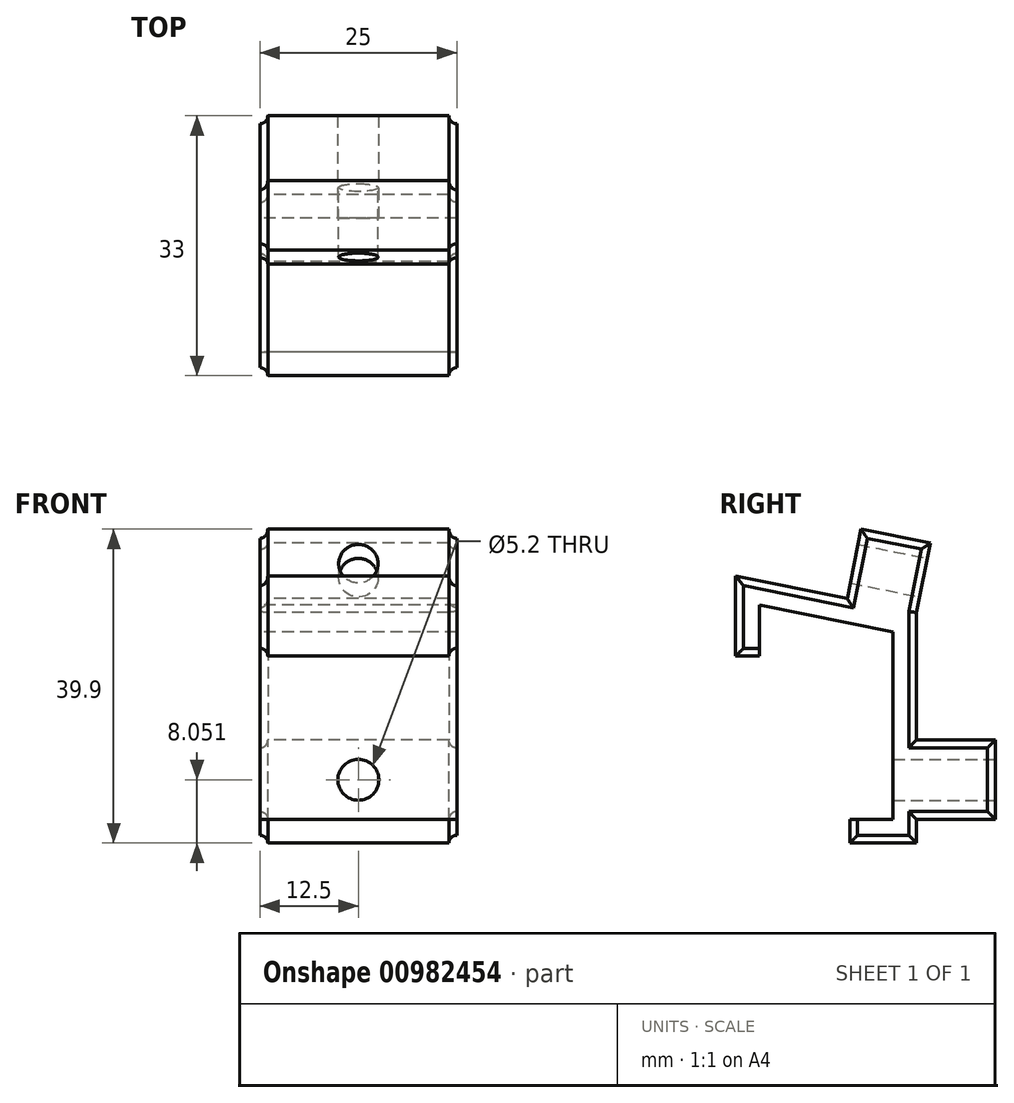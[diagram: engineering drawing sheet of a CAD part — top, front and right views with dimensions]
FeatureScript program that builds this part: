
annotation { "Feature Type Name" : "Feature", "Feature Type Description" : "" }
export const myFeature = defineFeature(function(context is Context, id is Id, definition is map)
    precondition{}
    {
        {
            var Q0;
            Q0=qCreatedBy(makeId("Right.planeOp"),FACE);
            var sketch = newSketch(context, id + "F0", { "sketchPlane" : qUnion([Q0])});
            skLineSegment(sketch, "E0.top", {"start": v(3.24, -5.36) * mm, "end": v(8.74, -5.36) * mm});
            skLineSegment(sketch, "E0.right", {"start": v(8.74, 18.5) * mm, "end": v(8.74, -5.36) * mm});
            skLineSegment(sketch, "E1", {"start": v(-5.7, 21.4) * mm, "end": v(8.74, 18.5) * mm});
            skLineSegment(sketch, "E2", {"start": v(8.74, -5.36) * mm, "end": v(3.24, -5.36) * mm});
            skLineSegment(sketch, "E3.0", {"start": v(11.74, -8.36) * mm, "end": v(3.24, -8.36) * mm});
            skLineSegment(sketch, "E3.1", {"start": v(11.74, 20.95) * mm, "end": v(11.74, -8.36) * mm});
            skLineSegment(sketch, "E3.2", {"start": v(-8.7, 25.05) * mm, "end": v(11.74, 20.95) * mm});
            skLineSegment(sketch, "E4", {"start": v(-8.7, 15.4) * mm, "end": v(-8.26, 15.4) * mm});
            skLineSegment(sketch, "E5", {"start": v(11.74, 20.95) * mm, "end": v(13.51, 29.77) * mm});
            skLineSegment(sketch, "E6", {"start": v(13.51, 29.77) * mm, "end": v(4.69, 31.54) * mm});
            skLineSegment(sketch, "E7", {"start": v(4.69, 31.54) * mm, "end": v(2.91, 22.72) * mm});
            skLineSegment(sketch, "E8", {"start": v(11.74, -5.36) * mm, "end": v(21.74, -5.36) * mm});
            skLineSegment(sketch, "E9", {"start": v(21.74, -5.36) * mm, "end": v(21.74, 4.74) * mm});
            skLineSegment(sketch, "E10", {"start": v(21.74, 4.74) * mm, "end": v(11.74, 4.74) * mm});
            skLineSegment(sketch, "E11", {"start": v(11.74, 4.74) * mm, "end": v(11.74, -5.36) * mm});
            skLineSegment(sketch, "E12", {"start": v(3.24, -5.36) * mm, "end": v(3.24, -8.36) * mm});
            skLineSegment(sketch, "E13", {"start": v(3.24, -8.36) * mm, "end": v(8.74, -8.36) * mm});
            skPoint(sketch, "E14.orphan", {"position": v(-7.76, -5.36) * mm});
            skLineSegment(sketch, "E15", {"start": v(-5.7, 21.4) * mm, "end": v(-8.26, 21.9) * mm});
            skLineSegment(sketch, "E16", {"start": v(-8.7, 25.05) * mm, "end": v(-11.26, 25.57) * mm});
            skLineSegment(sketch, "E17", {"start": v(-8.7, 15.4) * mm, "end": v(-11.26, 15.4) * mm});
            skLineSegment(sketch, "E18", {"start": v(-8.26, 21.9) * mm, "end": v(-8.26, 15.4) * mm});
            skLineSegment(sketch, "E19", {"start": v(-11.26, 25.57) * mm, "end": v(-11.26, 15.4) * mm});
            skLineSegment(sketch, "E20", {"start": v(-8.26, 21.9) * mm, "end": v(-8.26, 24.97) * mm});
            skSolve(sketch);
        }
        {
            var Q0;
            Q0 = qSketchRegion(id + "F0", true);
            extrude(context, id + "F1", {"entities" : qUnion([Q0]), "depth" : 25 * mm, "offsetDistance" : 25 * mm});
        }
        {
            var Q0;
            Q0=makeQuery(id+"F1.opExtrude","SWEPT_FACE",FACE,{"disambiguationData":[OSD([sQuery(id+"F0.wireOp",EDGE,"E5")])]});
            var sketch = newSketch(context, id + "F2", { "sketchPlane" : qUnion([Q0])});
            skLineSegment(sketch, "E21", {"start": v(-12.5, 23.66) * mm, "end": v(-12.5, 38.4) * mm, "construction": true});
            skPoint(sketch, "E21.startSnap0", {"position": v(-12.5, 22.85) * mm});
            skLineSegment(sketch, "E22", {"start": v(-25, 27.35) * mm, "end": v(3.97, 27.35) * mm, "construction": true});
            skCircle(sketch, "E23", {"center": v(-12.5, 27.35) * mm, "radius": 2.5 * mm});
            skLineSegment(sketch, "E24.bottom", {"start": v(-12.5, 31.85) * mm, "end": v(-10.5, 31.85) * mm});
            skLineSegment(sketch, "E24.top", {"start": v(-12.5, 31.85) * mm, "end": v(-10.5, 31.85) * mm});
            skLineSegment(sketch, "E24.left", {"start": v(-12.5, 31.85) * mm, "end": v(-12.5, 31.85) * mm});
            skLineSegment(sketch, "E24.right", {"start": v(-10.5, 31.85) * mm, "end": v(-10.5, 31.85) * mm});
            skLineSegment(sketch, "E25.top", {"start": v(-10.5, 28.85) * mm, "end": v(-10.5, 28.85) * mm});
            skLineSegment(sketch, "E25.left", {"start": v(-10.5, 31.85) * mm, "end": v(-10.5, 28.85) * mm});
            skLineSegment(sketch, "E25.right", {"start": v(-10.5, 31.85) * mm, "end": v(-10.5, 28.85) * mm});
            skLineSegment(sketch, "E26", {"start": v(-12.5, 31.85) * mm, "end": v(-14.5, 31.85) * mm});
            skLineSegment(sketch, "E27", {"start": v(-14.5, 31.85) * mm, "end": v(-14.5, 28.85) * mm});
            skSolve(sketch);
        }
        {
            var Q0;
            {var subQ0=sQuery(id+"F2.wireOp",EDGE,"E23");var subQ1=makeQuery(id+"F2.imprint","INTERSECT",VERTEX,{"derivedFrom":[subQ0,sQuery(id+"F2.wireOp",EDGE,"E25.right")]});Q0=makeQuery(id+"F2.imprint","IMPRINT",FACE,{"disambiguationData":[TD([[makeQuery(id+"F2.imprint","IMPRINT",EDGE,{"disambiguationData":[TD([[subQ1,-1.0]])],"derivedFrom":subQ0}),1.0]])]});}
            var Q1;
            Q1=makeQuery(id+"F2.imprint","IMPRINT",FACE,{"disambiguationData":[TD([[makeQuery(id+"F2.imprint","IMPRINT",EDGE,{"derivedFrom":sQuery(id+"F2.wireOp",EDGE,"E24.top")}),-1.0]])]});
            extrude(context, id + "F3", {"entities" : qUnion([Q0, Q1]), "operationType" : NewBodyOperationType.REMOVE, "endBound" : BoundingType.THROUGH_ALL, "oppositeDirection" : true, "depth" : 25 * mm, "offsetDistance" : 25 * mm});
        }
        {
            var Q0;
            Q0=makeQuery(id+"F1.opExtrude","SWEPT_FACE",FACE,{"disambiguationData":[OSD([sQuery(id+"F0.wireOp",EDGE,"E9")])]});
            var sketch = newSketch(context, id + "F4", { "sketchPlane" : qUnion([Q0])});
            skLineSegment(sketch, "E28", {"start": v(-12.5, 4.74) * mm, "end": v(-12.5, -5.36) * mm, "construction": true});
            skLineSegment(sketch, "E29", {"start": v(-25, -0.3) * mm, "end": v(0, -0.3) * mm, "construction": true});
            skCircle(sketch, "E30", {"center": v(-12.5, -0.3) * mm, "radius": 2.6 * mm});
            skSolve(sketch);
        }
        {
            var Q0;
            Q0=makeQuery(id+"F4.imprint","IMPRINT",FACE,{"disambiguationData":[TD([[makeQuery(id+"F4.imprint","IMPRINT",EDGE,{"derivedFrom":sQuery(id+"F4.wireOp",EDGE,"E30")}),1.0]])]});
            extrude(context, id + "F5", {"entities" : qUnion([Q0]), "operationType" : NewBodyOperationType.REMOVE, "endBound" : BoundingType.THROUGH_ALL, "oppositeDirection" : true, "depth" : 25 * mm, "offsetDistance" : 25 * mm});
        }
        {
            var Q0;
            Q0=makeQuery(id+"F1.opExtrude","CAP_FACE",FACE,{"disambiguationData":[OSD([sQuery(id+"F0.wireOp",EDGE,"E0.right"),sQuery(id+"F0.wireOp",EDGE,"E1"),sQuery(id+"F0.wireOp",EDGE,"n86n0oZb-3QEX-ZodZ-O8e6-zm0sU3kRzoy1"),sQuery(id+"F0.wireOp",EDGE,"E3.0"),sQuery(id+"F0.wireOp",EDGE,"E3.1"),sQuery(id+"F0.wireOp",EDGE,"E3.2"),sQuery(id+"F0.wireOp",EDGE,"E3.3"),sQuery(id+"F0.wireOp",EDGE,"E4"),sQuery(id+"F0.wireOp",EDGE,"E5"),sQuery(id+"F0.wireOp",EDGE,"E6"),sQuery(id+"F0.wireOp",EDGE,"E7"),sQuery(id+"F0.wireOp",EDGE,"E8"),sQuery(id+"F0.wireOp",EDGE,"E9"),sQuery(id+"F0.wireOp",EDGE,"E10"),sQuery(id+"F0.wireOp",EDGE,"E2"),sQuery(id+"F0.wireOp",EDGE,"E12"),sQuery(id+"F0.wireOp",EDGE,"E13")])],"isStart":true});
            var sketch = newSketch(context, id + "F6", { "sketchPlane" : qUnion([Q0])});
            skLineSegment(sketch, "E31", {"start": v(8.26, 15.4) * mm, "end": v(-2.91, 22.72) * mm});
            skLineSegment(sketch, "E32", {"start": v(-2.91, 22.72) * mm, "end": v(-2.91, 22.72) * mm});
            skLineSegment(sketch, "E33", {"start": v(-2.91, 22.72) * mm, "end": v(-4.69, 31.54) * mm});
            skLineSegment(sketch, "E34", {"start": v(-4.69, 31.54) * mm, "end": v(-13.51, 29.77) * mm});
            skLineSegment(sketch, "E35", {"start": v(-13.51, 29.77) * mm, "end": v(-11.74, 20.95) * mm});
            skLineSegment(sketch, "E36", {"start": v(-11.74, 20.95) * mm, "end": v(-11.74, 4.74) * mm});
            skLineSegment(sketch, "E37", {"start": v(-11.74, 4.74) * mm, "end": v(-21.74, 4.74) * mm});
            skLineSegment(sketch, "E38", {"start": v(-21.74, 4.74) * mm, "end": v(-21.74, -5.36) * mm});
            skLineSegment(sketch, "E39", {"start": v(-21.74, -5.36) * mm, "end": v(-11.74, -5.36) * mm});
            skLineSegment(sketch, "E40", {"start": v(-11.74, -5.36) * mm, "end": v(-11.74, -8.36) * mm});
            skLineSegment(sketch, "E41", {"start": v(-11.74, -8.36) * mm, "end": v(-3.24, -8.36) * mm});
            skLineSegment(sketch, "E42.0", {"start": v(-10.74, -7.36) * mm, "end": v(-3.24, -7.36) * mm});
            skLineSegment(sketch, "E42.1", {"start": v(-5.47, 30.37) * mm, "end": v(-12.33, 28.99) * mm});
            skLineSegment(sketch, "E42.2", {"start": v(-3.81, 22.11) * mm, "end": v(-5.47, 30.37) * mm});
            skLineSegment(sketch, "E42.3", {"start": v(-0.9, 20.2) * mm, "end": v(-3.81, 22.11) * mm});
            skLineSegment(sketch, "E42.4", {"start": v(6.44, 15.4) * mm, "end": v(-0.9, 20.2) * mm});
            skLineSegment(sketch, "E42.5", {"start": v(-12.33, 28.99) * mm, "end": v(-10.74, 21.05) * mm});
            skLineSegment(sketch, "E42.6", {"start": v(-10.74, 21.05) * mm, "end": v(-10.74, 3.74) * mm});
            skLineSegment(sketch, "E42.7", {"start": v(-10.74, 3.74) * mm, "end": v(-20.74, 3.74) * mm});
            skLineSegment(sketch, "E42.8", {"start": v(-20.74, 3.74) * mm, "end": v(-20.74, -4.36) * mm});
            skLineSegment(sketch, "E42.9", {"start": v(-20.74, -4.36) * mm, "end": v(-10.74, -4.36) * mm});
            skLineSegment(sketch, "E42.10", {"start": v(-10.74, -4.36) * mm, "end": v(-10.74, -7.36) * mm});
            skLineSegment(sketch, "E43", {"start": v(-3.24, -7.36) * mm, "end": v(-3.24, -8.36) * mm});
            skLineSegment(sketch, "E44", {"start": v(8.26, 15.4) * mm, "end": v(6.44, 15.4) * mm});
            skSolve(sketch);
        }
        {
            var Q0;
            Q0=makeQuery(id+"F6.imprint","IMPRINT",FACE,{"disambiguationData":[TD([[makeQuery(id+"F6.imprint","IMPRINT",EDGE,{"derivedFrom":sQuery(id+"F6.wireOp",EDGE,"E31")}),-1.0]])]});
            extrude(context, id + "F7", {"entities" : qUnion([Q0]), "operationType" : NewBodyOperationType.REMOVE, "oppositeDirection" : true, "depth" : 1 * mm, "offsetDistance" : 25 * mm});
        }
        {
            var Q0;
            Q0=makeQuery(id+"F1.opExtrude","CAP_FACE",FACE,{"disambiguationData":[OSD([sQuery(id+"F0.wireOp",EDGE,"E0.right"),sQuery(id+"F0.wireOp",EDGE,"E1"),sQuery(id+"F0.wireOp",EDGE,"E3.0"),sQuery(id+"F0.wireOp",EDGE,"E3.1"),sQuery(id+"F0.wireOp",EDGE,"E3.2"),sQuery(id+"F0.wireOp",EDGE,"E4"),sQuery(id+"F0.wireOp",EDGE,"E5"),sQuery(id+"F0.wireOp",EDGE,"E6"),sQuery(id+"F0.wireOp",EDGE,"E7"),sQuery(id+"F0.wireOp",EDGE,"E8"),sQuery(id+"F0.wireOp",EDGE,"E9"),sQuery(id+"F0.wireOp",EDGE,"E10"),sQuery(id+"F0.wireOp",EDGE,"E2"),sQuery(id+"F0.wireOp",EDGE,"E12"),sQuery(id+"F0.wireOp",EDGE,"E13"),sQuery(id+"F0.wireOp",EDGE,"E15"),sQuery(id+"F0.wireOp",EDGE,"E16"),sQuery(id+"F0.wireOp",EDGE,"E17"),sQuery(id+"F0.wireOp",EDGE,"E18"),sQuery(id+"F0.wireOp",EDGE,"E19")])],"isStart":false});
            var sketch = newSketch(context, id + "F8", { "sketchPlane" : qUnion([Q0])});
            skLineSegment(sketch, "E45", {"start": v(-8.26, 15.4) * mm, "end": v(-11.26, 15.4) * mm});
            skLineSegment(sketch, "E46", {"start": v(-11.26, 15.4) * mm, "end": v(-11.26, 25.57) * mm});
            skLineSegment(sketch, "E47", {"start": v(-11.26, 25.57) * mm, "end": v(2.91, 22.72) * mm});
            skLineSegment(sketch, "E48", {"start": v(2.91, 22.72) * mm, "end": v(4.69, 31.54) * mm});
            skLineSegment(sketch, "E49", {"start": v(4.69, 31.54) * mm, "end": v(13.51, 29.77) * mm});
            skLineSegment(sketch, "E50", {"start": v(13.51, 29.77) * mm, "end": v(11.74, 20.95) * mm});
            skLineSegment(sketch, "E51", {"start": v(11.74, 20.95) * mm, "end": v(11.74, 4.74) * mm});
            skLineSegment(sketch, "E52", {"start": v(11.74, 4.74) * mm, "end": v(21.74, 4.74) * mm});
            skLineSegment(sketch, "E53", {"start": v(21.74, 4.74) * mm, "end": v(21.74, -5.36) * mm});
            skLineSegment(sketch, "E54", {"start": v(21.74, -5.36) * mm, "end": v(11.74, -5.36) * mm});
            skLineSegment(sketch, "E55", {"start": v(11.74, -5.36) * mm, "end": v(11.74, -8.36) * mm});
            skLineSegment(sketch, "E56", {"start": v(11.74, -8.36) * mm, "end": v(3.24, -8.36) * mm});
            skLineSegment(sketch, "E57", {"start": v(3.24, -8.36) * mm, "end": v(3.24, -5.36) * mm});
            skLineSegment(sketch, "E58.0", {"start": v(4.24, -7.36) * mm, "end": v(4.24, -5.36) * mm});
            skLineSegment(sketch, "E58.1", {"start": v(10.74, -7.36) * mm, "end": v(4.24, -7.36) * mm});
            skLineSegment(sketch, "E58.2", {"start": v(10.74, -4.36) * mm, "end": v(10.74, -7.36) * mm});
            skLineSegment(sketch, "E58.3", {"start": v(3.7, 21.54) * mm, "end": v(5.47, 30.37) * mm});
            skLineSegment(sketch, "E58.4", {"start": v(-10.26, 24.35) * mm, "end": v(3.7, 21.54) * mm});
            skLineSegment(sketch, "E58.5", {"start": v(-10.26, 16.4) * mm, "end": v(-10.26, 24.35) * mm});
            skLineSegment(sketch, "E58.6", {"start": v(-8.26, 16.4) * mm, "end": v(-10.26, 16.4) * mm});
            skLineSegment(sketch, "E58.7", {"start": v(5.47, 30.37) * mm, "end": v(12.33, 28.99) * mm});
            skLineSegment(sketch, "E58.8", {"start": v(12.33, 28.99) * mm, "end": v(10.74, 21.05) * mm});
            skLineSegment(sketch, "E58.9", {"start": v(10.74, 21.05) * mm, "end": v(10.74, 3.74) * mm});
            skLineSegment(sketch, "E58.10", {"start": v(10.74, 3.74) * mm, "end": v(20.74, 3.74) * mm});
            skLineSegment(sketch, "E58.11", {"start": v(20.74, 3.74) * mm, "end": v(20.74, -4.36) * mm});
            skLineSegment(sketch, "E58.12", {"start": v(20.74, -4.36) * mm, "end": v(10.74, -4.36) * mm});
            skLineSegment(sketch, "E59", {"start": v(-8.26, 16.4) * mm, "end": v(-8.26, 15.4) * mm});
            skLineSegment(sketch, "E60", {"start": v(3.24, -5.36) * mm, "end": v(4.24, -5.36) * mm});
            skSolve(sketch);
        }
        {
            var Q0;
            Q0=makeQuery(id+"F8.imprint","IMPRINT",FACE,{"disambiguationData":[TD([[makeQuery(id+"F8.imprint","IMPRINT",EDGE,{"derivedFrom":sQuery(id+"F8.wireOp",EDGE,"E45")}),-1.0]])]});
            extrude(context, id + "F9", {"entities" : qUnion([Q0]), "operationType" : NewBodyOperationType.REMOVE, "oppositeDirection" : true, "depth" : 1 * mm, "offsetDistance" : 25 * mm});
        }
        {
            var Q0;
            Q0=makeQuery(id+"F1.opExtrude","CAP_FACE",FACE,{"disambiguationData":[OSD([sQuery(id+"F0.wireOp",EDGE,"E0.right"),sQuery(id+"F0.wireOp",EDGE,"E1"),sQuery(id+"F0.wireOp",EDGE,"E3.0"),sQuery(id+"F0.wireOp",EDGE,"E3.1"),sQuery(id+"F0.wireOp",EDGE,"E3.2"),sQuery(id+"F0.wireOp",EDGE,"E4"),sQuery(id+"F0.wireOp",EDGE,"E5"),sQuery(id+"F0.wireOp",EDGE,"E6"),sQuery(id+"F0.wireOp",EDGE,"E7"),sQuery(id+"F0.wireOp",EDGE,"E8"),sQuery(id+"F0.wireOp",EDGE,"E9"),sQuery(id+"F0.wireOp",EDGE,"E10"),sQuery(id+"F0.wireOp",EDGE,"E2"),sQuery(id+"F0.wireOp",EDGE,"E12"),sQuery(id+"F0.wireOp",EDGE,"E13"),sQuery(id+"F0.wireOp",EDGE,"E15"),sQuery(id+"F0.wireOp",EDGE,"E16"),sQuery(id+"F0.wireOp",EDGE,"E17"),sQuery(id+"F0.wireOp",EDGE,"E18"),sQuery(id+"F0.wireOp",EDGE,"E19")])],"isStart":true});
            var sketch = newSketch(context, id + "F10", { "sketchPlane" : qUnion([Q0])});
            skLineSegment(sketch, "E61", {"start": v(8.26, 15.4) * mm, "end": v(11.26, 15.4) * mm});
            skLineSegment(sketch, "E62", {"start": v(11.26, 15.4) * mm, "end": v(11.26, 25.57) * mm});
            skLineSegment(sketch, "E63", {"start": v(11.26, 25.57) * mm, "end": v(-2.91, 22.72) * mm});
            skLineSegment(sketch, "E64", {"start": v(-2.91, 22.72) * mm, "end": v(-4.69, 31.54) * mm});
            skLineSegment(sketch, "E65", {"start": v(-4.69, 31.54) * mm, "end": v(-13.51, 29.77) * mm});
            skLineSegment(sketch, "E66", {"start": v(-13.51, 29.77) * mm, "end": v(-11.74, 20.95) * mm});
            skLineSegment(sketch, "E67", {"start": v(-11.74, 20.95) * mm, "end": v(-11.74, 4.74) * mm});
            skLineSegment(sketch, "E68", {"start": v(-11.74, 4.74) * mm, "end": v(-21.74, 4.74) * mm});
            skLineSegment(sketch, "E69", {"start": v(-21.74, 4.74) * mm, "end": v(-21.74, -5.36) * mm});
            skLineSegment(sketch, "E70", {"start": v(-21.74, -5.36) * mm, "end": v(-11.74, -5.36) * mm});
            skLineSegment(sketch, "E71", {"start": v(-11.74, -5.36) * mm, "end": v(-11.74, -8.36) * mm});
            skLineSegment(sketch, "E72", {"start": v(-11.74, -8.36) * mm, "end": v(-3.24, -8.36) * mm});
            skLineSegment(sketch, "E73", {"start": v(-3.24, -8.36) * mm, "end": v(-3.24, -5.36) * mm});
            skLineSegment(sketch, "E74.0", {"start": v(-4.24, -7.36) * mm, "end": v(-4.24, -5.36) * mm});
            skLineSegment(sketch, "E74.1", {"start": v(-10.74, -7.36) * mm, "end": v(-4.24, -7.36) * mm});
            skLineSegment(sketch, "E74.2", {"start": v(-10.74, -4.36) * mm, "end": v(-10.74, -7.36) * mm});
            skLineSegment(sketch, "E74.3", {"start": v(-3.7, 21.54) * mm, "end": v(-5.47, 30.37) * mm});
            skLineSegment(sketch, "E74.4", {"start": v(10.26, 24.35) * mm, "end": v(-3.7, 21.54) * mm});
            skLineSegment(sketch, "E74.5", {"start": v(10.26, 16.4) * mm, "end": v(10.26, 24.35) * mm});
            skLineSegment(sketch, "E74.6", {"start": v(8.26, 16.4) * mm, "end": v(10.26, 16.4) * mm});
            skLineSegment(sketch, "E74.7", {"start": v(-5.47, 30.37) * mm, "end": v(-12.33, 28.99) * mm});
            skLineSegment(sketch, "E74.8", {"start": v(-12.33, 28.99) * mm, "end": v(-10.74, 21.05) * mm});
            skLineSegment(sketch, "E74.9", {"start": v(-10.74, 21.05) * mm, "end": v(-10.74, 3.74) * mm});
            skLineSegment(sketch, "E74.10", {"start": v(-10.74, 3.74) * mm, "end": v(-20.74, 3.74) * mm});
            skLineSegment(sketch, "E74.11", {"start": v(-20.74, 3.74) * mm, "end": v(-20.74, -4.36) * mm});
            skLineSegment(sketch, "E74.12", {"start": v(-20.74, -4.36) * mm, "end": v(-10.74, -4.36) * mm});
            skLineSegment(sketch, "E75.0", {"start": v(-3.74, 14.4) * mm, "end": v(3.26, 15.8) * mm});
            skLineSegment(sketch, "E75.1", {"start": v(-3.74, -0.36) * mm, "end": v(-3.74, 14.4) * mm});
            skLineSegment(sketch, "E75.2", {"start": v(1.76, -0.36) * mm, "end": v(-3.74, -0.36) * mm});
            skLineSegment(sketch, "E75.3", {"start": v(1.76, -13.36) * mm, "end": v(1.76, -0.36) * mm});
            skLineSegment(sketch, "E75.4", {"start": v(-16.74, -13.36) * mm, "end": v(1.76, -13.36) * mm});
            skLineSegment(sketch, "E75.5", {"start": v(3.26, 15.8) * mm, "end": v(3.26, 10.4) * mm});
            skLineSegment(sketch, "E75.6", {"start": v(-16.74, -10.36) * mm, "end": v(-16.74, -13.36) * mm});
            skLineSegment(sketch, "E75.7", {"start": v(1, 28.6) * mm, "end": v(-0.77, 37.43) * mm});
            skLineSegment(sketch, "E75.8", {"start": v(16.26, 31.67) * mm, "end": v(1, 28.6) * mm});
            skLineSegment(sketch, "E75.9", {"start": v(16.26, 10.4) * mm, "end": v(16.26, 31.67) * mm});
            skLineSegment(sketch, "E75.10", {"start": v(3.26, 10.4) * mm, "end": v(16.26, 10.4) * mm});
            skLineSegment(sketch, "E75.11", {"start": v(-0.77, 37.43) * mm, "end": v(-19.4, 33.69) * mm});
            skLineSegment(sketch, "E75.12", {"start": v(-19.4, 33.69) * mm, "end": v(-16.74, 20.45) * mm});
            skLineSegment(sketch, "E75.13", {"start": v(-16.74, 20.45) * mm, "end": v(-16.74, 9.74) * mm});
            skLineSegment(sketch, "E75.14", {"start": v(-16.74, 9.74) * mm, "end": v(-26.74, 9.74) * mm});
            skLineSegment(sketch, "E75.15", {"start": v(-26.74, 9.74) * mm, "end": v(-26.74, -10.36) * mm});
            skLineSegment(sketch, "E75.16", {"start": v(-26.74, -10.36) * mm, "end": v(-16.74, -10.36) * mm});
            skLineSegment(sketch, "E76", {"start": v(8.26, 16.4) * mm, "end": v(8.26, 15.4) * mm});
            skLineSegment(sketch, "E77", {"start": v(-4.24, -5.36) * mm, "end": v(-3.24, -5.36) * mm});
            skSolve(sketch);
        }
        {
            var Q0;
            Q0=makeQuery(id+"F10.imprint","IMPRINT",FACE,{"disambiguationData":[TD([[makeQuery(id+"F10.imprint","IMPRINT",EDGE,{"derivedFrom":sQuery(id+"F10.wireOp",EDGE,"E61")}),1.0]])]});
            extrude(context, id + "F11", {"entities" : qUnion([Q0]), "operationType" : NewBodyOperationType.REMOVE, "oppositeDirection" : true, "depth" : 1 * mm, "offsetDistance" : 25 * mm});
        }
        {
            var Q0;
            Q0=makeQuery(id+"F9.boolean.opBoolean","COPY",EDGE,{"derivedFrom":makeQuery(id+"F9.opExtrude","CAP_EDGE",EDGE,{"disambiguationData":[OSD([sQuery(id+"F8.wireOp",EDGE,"E58.0")])],"isStart":false})});
            var Q1;
            Q1=makeQuery(id+"F9.boolean.opBoolean","COPY",EDGE,{"derivedFrom":makeQuery(id+"F9.opExtrude","CAP_EDGE",EDGE,{"disambiguationData":[OSD([sQuery(id+"F8.wireOp",EDGE,"E58.1")])],"isStart":false})});
            var Q2;
            Q2=makeQuery(id+"F9.boolean.opBoolean","COPY",EDGE,{"derivedFrom":makeQuery(id+"F9.opExtrude","CAP_EDGE",EDGE,{"disambiguationData":[OSD([sQuery(id+"F8.wireOp",EDGE,"E58.12")])],"isStart":false})});
            var Q3;
            Q3=makeQuery(id+"F9.boolean.opBoolean","COPY",EDGE,{"derivedFrom":makeQuery(id+"F9.opExtrude","CAP_EDGE",EDGE,{"disambiguationData":[OSD([sQuery(id+"F8.wireOp",EDGE,"E58.2")])],"isStart":false})});
            var Q4;
            Q4=makeQuery(id+"F9.boolean.opBoolean","COPY",EDGE,{"derivedFrom":makeQuery(id+"F9.opExtrude","CAP_EDGE",EDGE,{"disambiguationData":[OSD([sQuery(id+"F8.wireOp",EDGE,"E58.11")])],"isStart":false})});
            var Q5;
            Q5=makeQuery(id+"F9.boolean.opBoolean","COPY",EDGE,{"derivedFrom":makeQuery(id+"F9.opExtrude","CAP_EDGE",EDGE,{"disambiguationData":[OSD([sQuery(id+"F8.wireOp",EDGE,"E58.9")])],"isStart":false})});
            var Q6;
            Q6=makeQuery(id+"F9.boolean.opBoolean","COPY",EDGE,{"derivedFrom":makeQuery(id+"F9.opExtrude","CAP_EDGE",EDGE,{"disambiguationData":[OSD([sQuery(id+"F8.wireOp",EDGE,"E58.10")])],"isStart":false})});
            var Q7;
            Q7=makeQuery(id+"F9.boolean.opBoolean","COPY",EDGE,{"derivedFrom":makeQuery(id+"F9.opExtrude","CAP_EDGE",EDGE,{"disambiguationData":[OSD([sQuery(id+"F8.wireOp",EDGE,"E58.8")])],"isStart":false})});
            var Q8;
            Q8=makeQuery(id+"F9.boolean.opBoolean","COPY",EDGE,{"derivedFrom":makeQuery(id+"F9.opExtrude","CAP_EDGE",EDGE,{"disambiguationData":[OSD([sQuery(id+"F8.wireOp",EDGE,"E58.7")])],"isStart":false})});
            var Q9;
            Q9=makeQuery(id+"F9.boolean.opBoolean","COPY",EDGE,{"derivedFrom":makeQuery(id+"F9.opExtrude","CAP_EDGE",EDGE,{"disambiguationData":[OSD([sQuery(id+"F8.wireOp",EDGE,"E58.4")])],"isStart":false})});
            var Q10;
            Q10=makeQuery(id+"F9.boolean.opBoolean","COPY",EDGE,{"derivedFrom":makeQuery(id+"F9.opExtrude","CAP_EDGE",EDGE,{"disambiguationData":[OSD([sQuery(id+"F8.wireOp",EDGE,"E58.3")])],"isStart":false})});
            var Q11;
            Q11=makeQuery(id+"F9.boolean.opBoolean","COPY",EDGE,{"derivedFrom":makeQuery(id+"F9.opExtrude","CAP_EDGE",EDGE,{"disambiguationData":[OSD([sQuery(id+"F8.wireOp",EDGE,"E58.5")])],"isStart":false})});
            var Q12;
            Q12=makeQuery(id+"F9.boolean.opBoolean","COPY",EDGE,{"derivedFrom":makeQuery(id+"F9.opExtrude","CAP_EDGE",EDGE,{"disambiguationData":[OSD([sQuery(id+"F8.wireOp",EDGE,"E58.6")])],"isStart":false})});
            fillet(context, id + "F12", {"entities" : qUnion([Q0, Q1, Q2, Q3, Q4, Q5, Q6, Q7, Q8, Q9, Q10, Q11, Q12]), "radius" : 1 * mm, "tangentPropagation" : true, "allowEdgeOverflow" : false});
        }
        {
            var Q0;
            Q0=makeQuery(id+"F11.boolean.opBoolean","COPY",EDGE,{"derivedFrom":makeQuery(id+"F11.opExtrude","CAP_EDGE",EDGE,{"disambiguationData":[OSD([sQuery(id+"F10.wireOp",EDGE,"E74.0")])],"isStart":false})});
            var Q1;
            Q1=makeQuery(id+"F11.boolean.opBoolean","COPY",EDGE,{"derivedFrom":makeQuery(id+"F11.opExtrude","CAP_EDGE",EDGE,{"disambiguationData":[OSD([sQuery(id+"F10.wireOp",EDGE,"E74.1")])],"isStart":false})});
            var Q2;
            Q2=makeQuery(id+"F11.boolean.opBoolean","COPY",EDGE,{"derivedFrom":makeQuery(id+"F11.opExtrude","CAP_EDGE",EDGE,{"disambiguationData":[OSD([sQuery(id+"F10.wireOp",EDGE,"E74.12")])],"isStart":false})});
            var Q3;
            Q3=makeQuery(id+"F11.boolean.opBoolean","COPY",EDGE,{"derivedFrom":makeQuery(id+"F11.opExtrude","CAP_EDGE",EDGE,{"disambiguationData":[OSD([sQuery(id+"F10.wireOp",EDGE,"E74.2")])],"isStart":false})});
            var Q4;
            Q4=makeQuery(id+"F11.boolean.opBoolean","COPY",EDGE,{"derivedFrom":makeQuery(id+"F11.opExtrude","CAP_EDGE",EDGE,{"disambiguationData":[OSD([sQuery(id+"F10.wireOp",EDGE,"E74.11")])],"isStart":false})});
            var Q5;
            Q5=makeQuery(id+"F11.boolean.opBoolean","COPY",EDGE,{"derivedFrom":makeQuery(id+"F11.opExtrude","CAP_EDGE",EDGE,{"disambiguationData":[OSD([sQuery(id+"F10.wireOp",EDGE,"E74.9")])],"isStart":false})});
            var Q6;
            Q6=makeQuery(id+"F11.boolean.opBoolean","COPY",EDGE,{"derivedFrom":makeQuery(id+"F11.opExtrude","CAP_EDGE",EDGE,{"disambiguationData":[OSD([sQuery(id+"F10.wireOp",EDGE,"E74.10")])],"isStart":false})});
            var Q7;
            Q7=makeQuery(id+"F11.boolean.opBoolean","COPY",EDGE,{"derivedFrom":makeQuery(id+"F11.opExtrude","CAP_EDGE",EDGE,{"disambiguationData":[OSD([sQuery(id+"F10.wireOp",EDGE,"E74.8")])],"isStart":false})});
            var Q8;
            Q8=makeQuery(id+"F11.boolean.opBoolean","COPY",EDGE,{"derivedFrom":makeQuery(id+"F11.opExtrude","CAP_EDGE",EDGE,{"disambiguationData":[OSD([sQuery(id+"F10.wireOp",EDGE,"E74.7")])],"isStart":false})});
            var Q9;
            Q9=makeQuery(id+"F11.boolean.opBoolean","COPY",EDGE,{"derivedFrom":makeQuery(id+"F11.opExtrude","CAP_EDGE",EDGE,{"disambiguationData":[OSD([sQuery(id+"F10.wireOp",EDGE,"E74.4")])],"isStart":false})});
            var Q10;
            Q10=makeQuery(id+"F11.boolean.opBoolean","COPY",EDGE,{"derivedFrom":makeQuery(id+"F11.opExtrude","CAP_EDGE",EDGE,{"disambiguationData":[OSD([sQuery(id+"F10.wireOp",EDGE,"E74.3")])],"isStart":false})});
            var Q11;
            Q11=makeQuery(id+"F11.boolean.opBoolean","COPY",EDGE,{"derivedFrom":makeQuery(id+"F11.opExtrude","CAP_EDGE",EDGE,{"disambiguationData":[OSD([sQuery(id+"F10.wireOp",EDGE,"E74.5")])],"isStart":false})});
            var Q12;
            Q12=makeQuery(id+"F11.boolean.opBoolean","COPY",EDGE,{"derivedFrom":makeQuery(id+"F11.opExtrude","CAP_EDGE",EDGE,{"disambiguationData":[OSD([sQuery(id+"F10.wireOp",EDGE,"E74.6")])],"isStart":false})});
            fillet(context, id + "F13", {"entities" : qUnion([Q0, Q1, Q2, Q3, Q4, Q5, Q6, Q7, Q8, Q9, Q10, Q11, Q12]), "radius" : 1 * mm, "tangentPropagation" : true, "allowEdgeOverflow" : false});
        }
    });
